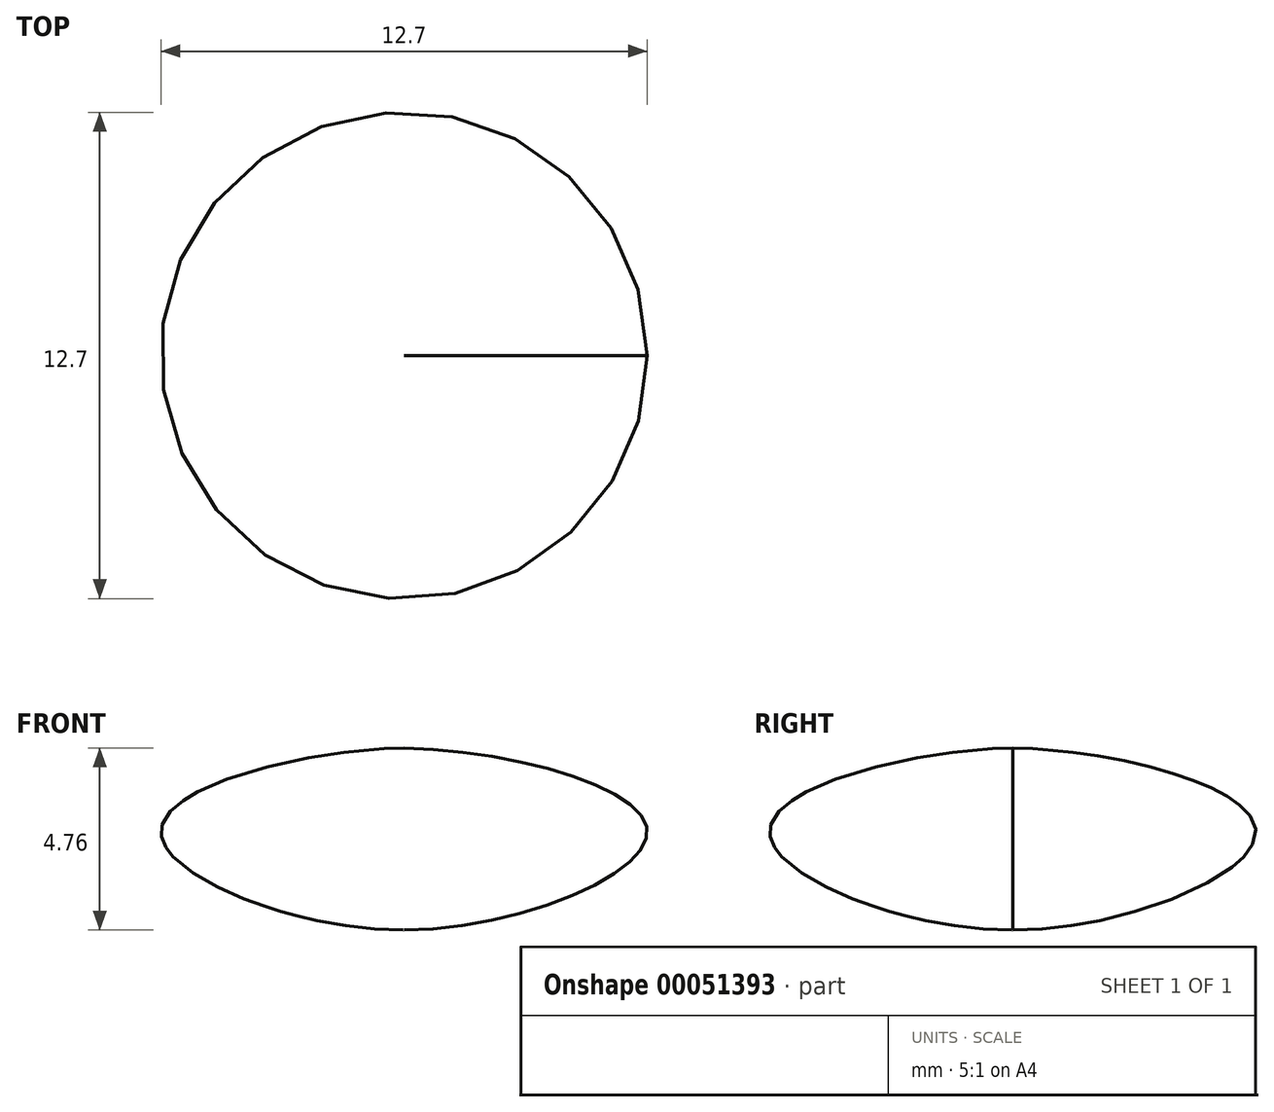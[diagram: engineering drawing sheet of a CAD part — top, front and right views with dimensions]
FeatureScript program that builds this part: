
annotation { "Feature Type Name" : "Feature", "Feature Type Description" : "" }
export const myFeature = defineFeature(function(context is Context, id is Id, definition is map)
    precondition{}
    {
        {
            var Q0;
            Q0=qCreatedBy(makeId("Front.planeOp"),FACE);
            var sketch = newSketch(context, id + "F0", { "sketchPlane" : qUnion([Q0])});
            skFitSpline(sketch, "E0", {"points": [v(0, 4.76) * mm, v(6.35, 2.58) * mm, v(0, 0) * mm], "startDerivative": vector(17.18, -0.43) * mm, "endDerivative": vector(-17, 0) * mm});
            skLineSegment(sketch, "E1", {"start": v(0, 4.76) * mm, "end": v(0, 0) * mm});
            skSolve(sketch);
        }
        {
            var Q0;
            Q0=makeQuery(id+"F0.imprint","IMPRINT",FACE,{"disambiguationData":[TD([[makeQuery(id+"F0.imprint","IMPRINT",EDGE,{"derivedFrom":sQuery(id+"F0.wireOp",EDGE,"E0")}),-1.0]])]});
            var Q1;
            Q1=sQuery(id+"F0.wireOp",EDGE,"E1");
            revolve(context, id + "F1", {"entities" : qUnion([Q0]), "axis" : qUnion([Q1]), "revolveType" : RevolveType.FULL});
        }
    });
